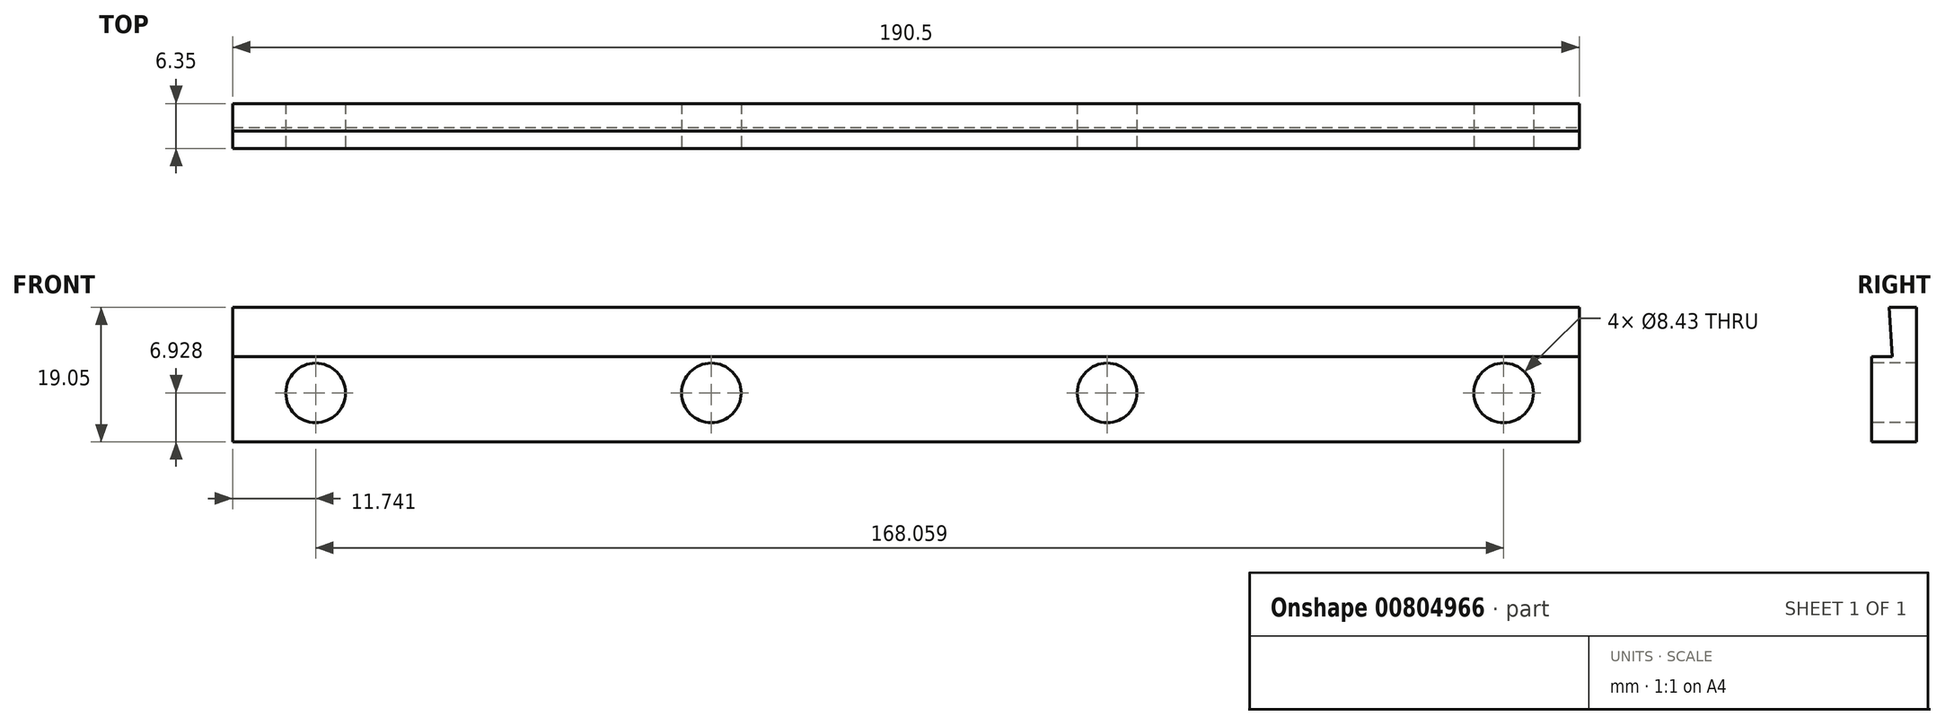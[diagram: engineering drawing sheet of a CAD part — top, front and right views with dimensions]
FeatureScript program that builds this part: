
annotation { "Feature Type Name" : "Feature", "Feature Type Description" : "" }
export const myFeature = defineFeature(function(context is Context, id is Id, definition is map)
    precondition{}
    {
        {
            var Q0;
            Q0=qCreatedBy(makeId("Front.planeOp"),FACE);
            var sketch = newSketch(context, id + "F0", { "sketchPlane" : qUnion([Q0])});
            skLineSegment(sketch, "E0.bottom", {"start": v(0, 0) * mm, "end": v(190.5, 0) * mm});
            skLineSegment(sketch, "E0.top", {"start": v(0, 19.05) * mm, "end": v(190.5, 19.05) * mm});
            skLineSegment(sketch, "E0.left", {"start": v(0, 0) * mm, "end": v(0, 19.05) * mm});
            skLineSegment(sketch, "E0.right", {"start": v(190.5, 0) * mm, "end": v(190.5, 19.05) * mm});
            skSolve(sketch);
        }
        {
            var Q0;
            Q0 = qSketchRegion(id + "F0", true);
            extrude(context, id + "F1", {"entities" : qUnion([Q0]), "depth" : 6.35 * mm, "offsetDistance" : 25.4 * mm});
        }
        {
            var Q0;
            Q0=makeQuery(id+"F1.opExtrude","CAP_FACE",FACE,{"disambiguationData":[OSD([sQuery(id+"F0.wireOp",EDGE,"E0.bottom"),sQuery(id+"F0.wireOp",EDGE,"E0.top"),sQuery(id+"F0.wireOp",EDGE,"E0.left"),sQuery(id+"F0.wireOp",EDGE,"E0.right")])],"isStart":false});
            var sketch = newSketch(context, id + "F2", { "sketchPlane" : qUnion([Q0])});
            skCircle(sketch, "E1", {"center": v(11.74, 6.93) * mm, "radius": 4.38 * mm, "construction": true});
            skCircle(sketch, "E2", {"center": v(67.72, 6.93) * mm, "radius": 4.38 * mm, "construction": true});
            skCircle(sketch, "E3", {"center": v(123.7, 6.93) * mm, "radius": 4.38 * mm, "construction": true});
            skCircle(sketch, "E4", {"center": v(179.8, 6.93) * mm, "radius": 4.38 * mm, "construction": true});
            skSolve(sketch);
        }
        {
            var Q0;
            Q0=sQuery(id+"F2.wireOp",VERTEX,"E1.center");
            var Q1;
            Q1=sQuery(id+"F2.wireOp",VERTEX,"E2.center");
            var Q2;
            Q2=sQuery(id+"F2.wireOp",VERTEX,"E3.center");
            var Q3;
            Q3=sQuery(id+"F2.wireOp",VERTEX,"E4.center");
            var Q4;
            Q4=makeQuery(id+"F1.opExtrude","SWEPT_BODY",BODY,{"disambiguationData":[OSD([sQuery(id+"F0.wireOp",EDGE,"E0.bottom"),sQuery(id+"F0.wireOp",EDGE,"E0.top"),sQuery(id+"F0.wireOp",EDGE,"E0.left"),sQuery(id+"F0.wireOp",EDGE,"E0.right")])]});
            hole(context, id + "F3", {"style" : HoleStyle.SIMPLE, "endStyle" : HoleEndStyle.THROUGH, "standardTappedOrClearance" : lookupTablePath({ "fit" : "Free", "standard" : "ANSI", "size" : "5/16", "type" : "Clearance" }), "standardBlindInLast" : lookupTablePath({ "fit" : "Free", "standard" : "ANSI", "engagement" : "75%", "pitch" : "18 tpi", "size" : "5/16", "type" : "Clearance & tapped" }), "holeDiameter" : 8.43 * mm, "majorDiameter" : 7.94 * mm, "isTappedThrough" : true, "tappedDepth" : 21.17 * mm, "tapClearance" : 3, "startFromSketch" : true, "locations" : qUnion([Q0, Q1, Q2, Q3]), "scope" : qUnion([Q4])});
        }
        {
            var Q0;
            Q0=makeQuery(id+"F1.opExtrude","SWEPT_FACE",FACE,{"disambiguationData":[OSD([sQuery(id+"F0.wireOp",EDGE,"E0.right")])]});
            var sketch = newSketch(context, id + "F4", { "sketchPlane" : qUnion([Q0])});
            skLineSegment(sketch, "E5", {"start": v(-6.35, 12.04) * mm, "end": v(-3.4, 12.04) * mm});
            skLineSegment(sketch, "E6", {"start": v(-3.4, 12.04) * mm, "end": v(-3.89, 19.05) * mm});
            skLineSegment(sketch, "E7", {"start": v(-3.89, 19.05) * mm, "end": v(-6.35, 19.05) * mm});
            skLineSegment(sketch, "E8", {"start": v(-6.35, 19.05) * mm, "end": v(-6.35, 12.04) * mm});
            skSolve(sketch);
        }
        {
            var Q0;
            Q0 = qSketchRegion(id + "F4", true);
            extrude(context, id + "F5", {"entities" : qUnion([Q0]), "operationType" : NewBodyOperationType.REMOVE, "endBound" : BoundingType.THROUGH_ALL, "oppositeDirection" : true, "depth" : 25.4 * mm, "offsetDistance" : 25.4 * mm});
        }
    });
